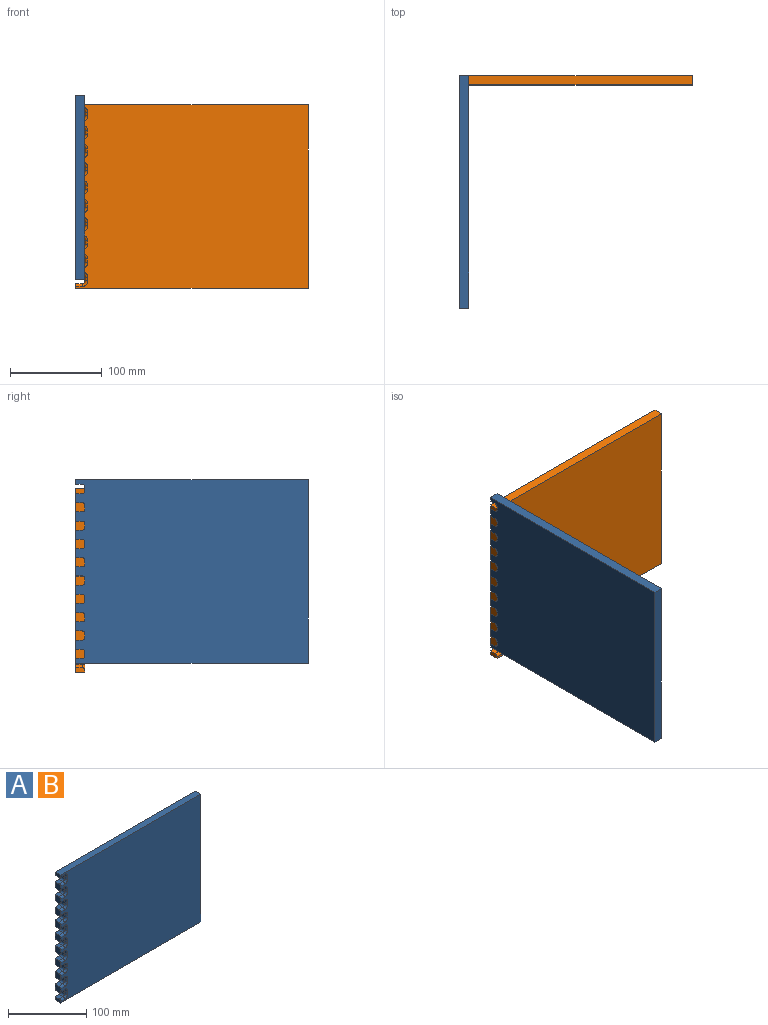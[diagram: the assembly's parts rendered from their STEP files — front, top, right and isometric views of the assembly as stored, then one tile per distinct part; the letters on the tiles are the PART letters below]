
ASSEMBLY  parts=2 mates=1
PART A: 116 faces, bbox 253.6x10x201.6 mm
  f0: plane 10x10mm, normal (-1,0,0), area 96.1mm2, adj f7,f8,f13,f21,f100,f101
  f1: cylinder r=3mm len=7mm, axis (0,1,0), area 33mm2, adj f3,f9,f10,f101
  f2: cylinder r=3mm len=7mm, axis (1,0,0), area 33mm2, adj f3,f10,f99,f100
  f3: torus R=6mm, axis (0,-1,0), area 30.3mm2, adj f1,f2,f5,f100
  f4: cylinder r=3mm len=7mm, axis (0,-1,0), area 33mm2, adj f6,f8,f9,f101
  f5: cylinder r=3mm len=4mm, axis (0,0,-1), area 18.8mm2, adj f3,f6,f9,f100
  f6: torus R=6mm, axis (0,-1,0), area 30.3mm2, adj f4,f5,f7,f100
  f7: cylinder r=3mm len=7mm, axis (-1,0,0), area 33mm2, adj f0,f6,f8,f100
  f8: plane 7x7mm, normal (0,0,1), area 49mm2, adj f0,f4,f7,f101
  f9: plane 7x4mm, normal (-1,0,0), area 28mm2, adj f1,f4,f5,f101
  f10: plane 7x7mm, normal (0,0,-1), area 49mm2, adj f1,f2,f99,f101
  f11: plane 10x10mm, normal (-1,0,0), area 96.1mm2, adj f18,f19,f24,f32,f100,f101
  f12: cylinder r=3mm len=7mm, axis (0,1,0), area 33mm2, adj f14,f20,f21,f101
  f13: cylinder r=3mm len=7mm, axis (1,0,0), area 33mm2, adj f0,f14,f21,f100
  f14: torus R=6mm, axis (0,-1,0), area 30.3mm2, adj f12,f13,f16,f100
  f15: cylinder r=3mm len=7mm, axis (0,-1,0), area 33mm2, adj f17,f19,f20,f101
  f16: cylinder r=3mm len=4mm, axis (0,0,-1), area 18.8mm2, adj f14,f17,f20,f100
  f17: torus R=6mm, axis (0,-1,0), area 30.3mm2, adj f15,f16,f18,f100
  f18: cylinder r=3mm len=7mm, axis (-1,0,0), area 33mm2, adj f11,f17,f19,f100
  f19: plane 7x7mm, normal (0,0,1), area 49mm2, adj f11,f15,f18,f101
  f20: plane 7x4mm, normal (-1,0,0), area 28mm2, adj f12,f15,f16,f101
  f21: plane 7x7mm, normal (0,0,-1), area 49mm2, adj f0,f12,f13,f101
  f22: plane 10x10mm, normal (-1,0,0), area 96.1mm2, adj f29,f30,f35,f43,f100,f101
  f23: cylinder r=3mm len=7mm, axis (0,1,0), area 33mm2, adj f25,f31,f32,f101
  f24: cylinder r=3mm len=7mm, axis (1,0,0), area 33mm2, adj f11,f25,f32,f100
  f25: torus R=6mm, axis (0,-1,0), area 30.3mm2, adj f23,f24,f27,f100
  f26: cylinder r=3mm len=7mm, axis (0,-1,0), area 33mm2, adj f28,f30,f31,f101
  f27: cylinder r=3mm len=4mm, axis (0,0,-1), area 18.8mm2, adj f25,f28,f31,f100
  f28: torus R=6mm, axis (0,-1,0), area 30.3mm2, adj f26,f27,f29,f100
  f29: cylinder r=3mm len=7mm, axis (-1,0,0), area 33mm2, adj f22,f28,f30,f100
  f30: plane 7x7mm, normal (0,0,1), area 49mm2, adj f22,f26,f29,f101
  f31: plane 7x4mm, normal (-1,0,0), area 28mm2, adj f23,f26,f27,f101
  f32: plane 7x7mm, normal (0,0,-1), area 49mm2, adj f11,f23,f24,f101
  f33: plane 10x10mm, normal (-1,0,0), area 96.1mm2, adj f40,f41,f46,f54,f100,f101
  f34: cylinder r=3mm len=7mm, axis (0,1,0), area 33mm2, adj f36,f42,f43,f101
  f35: cylinder r=3mm len=7mm, axis (1,0,0), area 33mm2, adj f22,f36,f43,f100
  f36: torus R=6mm, axis (0,-1,0), area 30.3mm2, adj f34,f35,f38,f100
  f37: cylinder r=3mm len=7mm, axis (0,-1,0), area 33mm2, adj f39,f41,f42,f101
  f38: cylinder r=3mm len=4mm, axis (0,0,-1), area 18.8mm2, adj f36,f39,f42,f100
  f39: torus R=6mm, axis (0,-1,0), area 30.3mm2, adj f37,f38,f40,f100
  f40: cylinder r=3mm len=7mm, axis (-1,0,0), area 33mm2, adj f33,f39,f41,f100
  f41: plane 7x7mm, normal (0,0,1), area 49mm2, adj f33,f37,f40,f101
  f42: plane 7x4mm, normal (-1,0,0), area 28mm2, adj f34,f37,f38,f101
  f43: plane 7x7mm, normal (0,0,-1), area 49mm2, adj f22,f34,f35,f101
  f44: plane 10x10mm, normal (-1,0,0), area 96.1mm2, adj f51,f52,f57,f65,f100,f101
  f45: cylinder r=3mm len=7mm, axis (0,1,0), area 33mm2, adj f47,f53,f54,f101
  f46: cylinder r=3mm len=7mm, axis (1,0,0), area 33mm2, adj f33,f47,f54,f100
  f47: torus R=6mm, axis (0,-1,0), area 30.3mm2, adj f45,f46,f49,f100
  f48: cylinder r=3mm len=7mm, axis (0,-1,0), area 33mm2, adj f50,f52,f53,f101
  f49: cylinder r=3mm len=4mm, axis (0,0,-1), area 18.8mm2, adj f47,f50,f53,f100
  f50: torus R=6mm, axis (0,-1,0), area 30.3mm2, adj f48,f49,f51,f100
  f51: cylinder r=3mm len=7mm, axis (-1,0,0), area 33mm2, adj f44,f50,f52,f100
  f52: plane 7x7mm, normal (0,0,1), area 49mm2, adj f44,f48,f51,f101
  f53: plane 7x4mm, normal (-1,0,0), area 28mm2, adj f45,f48,f49,f101
  f54: plane 7x7mm, normal (0,0,-1), area 49mm2, adj f33,f45,f46,f101
  f55: plane 10x10mm, normal (-1,0,0), area 96.1mm2, adj f62,f63,f68,f76,f100,f101
  f56: cylinder r=3mm len=7mm, axis (0,1,0), area 33mm2, adj f58,f64,f65,f101
  f57: cylinder r=3mm len=7mm, axis (1,0,0), area 33mm2, adj f44,f58,f65,f100
  f58: torus R=6mm, axis (0,-1,0), area 30.3mm2, adj f56,f57,f60,f100
  f59: cylinder r=3mm len=7mm, axis (0,-1,0), area 33mm2, adj f61,f63,f64,f101
  f60: cylinder r=3mm len=4mm, axis (0,0,-1), area 18.8mm2, adj f58,f61,f64,f100
  f61: torus R=6mm, axis (0,-1,0), area 30.3mm2, adj f59,f60,f62,f100
  f62: cylinder r=3mm len=7mm, axis (-1,0,0), area 33mm2, adj f55,f61,f63,f100
  f63: plane 7x7mm, normal (0,0,1), area 49mm2, adj f55,f59,f62,f101
  f64: plane 7x4mm, normal (-1,0,0), area 28mm2, adj f56,f59,f60,f101
  f65: plane 7x7mm, normal (0,0,-1), area 49mm2, adj f44,f56,f57,f101
  f66: plane 10x10mm, normal (-1,0,0), area 96.1mm2, adj f73,f74,f79,f87,f100,f101
  f67: cylinder r=3mm len=7mm, axis (0,1,0), area 33mm2, adj f69,f75,f76,f101
  f68: cylinder r=3mm len=7mm, axis (1,0,0), area 33mm2, adj f55,f69,f76,f100
  f69: torus R=6mm, axis (0,-1,0), area 30.3mm2, adj f67,f68,f71,f100
  f70: cylinder r=3mm len=7mm, axis (0,-1,0), area 33mm2, adj f72,f74,f75,f101
  f71: cylinder r=3mm len=4mm, axis (0,0,-1), area 18.8mm2, adj f69,f72,f75,f100
  f72: torus R=6mm, axis (0,-1,0), area 30.3mm2, adj f70,f71,f73,f100
  f73: cylinder r=3mm len=7mm, axis (-1,0,0), area 33mm2, adj f66,f72,f74,f100
  f74: plane 7x7mm, normal (0,0,1), area 49mm2, adj f66,f70,f73,f101
  f75: plane 7x4mm, normal (-1,0,0), area 28mm2, adj f67,f70,f71,f101
  f76: plane 7x7mm, normal (0,0,-1), area 49mm2, adj f55,f67,f68,f101
  f77: plane 10x10mm, normal (-1,0,0), area 96.1mm2, adj f84,f85,f90,f98,f100,f101
  f78: cylinder r=3mm len=7mm, axis (0,1,0), area 33mm2, adj f80,f86,f87,f101
  f79: cylinder r=3mm len=7mm, axis (1,0,0), area 33mm2, adj f66,f80,f87,f100
  f80: torus R=6mm, axis (0,-1,0), area 30.3mm2, adj f78,f79,f82,f100
  f81: cylinder r=3mm len=7mm, axis (0,-1,0), area 33mm2, adj f83,f85,f86,f101
  f82: cylinder r=3mm len=4mm, axis (0,0,-1), area 18.8mm2, adj f80,f83,f86,f100
  f83: torus R=6mm, axis (0,-1,0), area 30.3mm2, adj f81,f82,f84,f100
  f84: cylinder r=3mm len=7mm, axis (-1,0,0), area 33mm2, adj f77,f83,f85,f100
  f85: plane 7x7mm, normal (0,0,1), area 49mm2, adj f77,f81,f84,f101
  f86: plane 7x4mm, normal (-1,0,0), area 28mm2, adj f78,f81,f82,f101
  f87: plane 7x7mm, normal (0,0,-1), area 49mm2, adj f66,f78,f79,f101
  f88: plane 10x10mm, normal (-1,0,0), area 96.1mm2, adj f95,f96,f100,f101,f108,f110
  f89: cylinder r=3mm len=7mm, axis (0,1,0), area 33mm2, adj f91,f97,f98,f101
  f90: cylinder r=3mm len=7mm, axis (1,0,0), area 33mm2, adj f77,f91,f98,f100
  f91: torus R=6mm, axis (0,-1,0), area 30.3mm2, adj f89,f90,f93,f100
  f92: cylinder r=3mm len=7mm, axis (0,-1,0), area 33mm2, adj f94,f96,f97,f101
  f93: cylinder r=3mm len=4mm, axis (0,0,-1), area 18.8mm2, adj f91,f94,f97,f100
  f94: torus R=6mm, axis (0,-1,0), area 30.3mm2, adj f92,f93,f95,f100
  f95: cylinder r=3mm len=7mm, axis (-1,0,0), area 33mm2, adj f88,f94,f96,f100
  f96: plane 7x7mm, normal (0,0,1), area 49mm2, adj f88,f92,f95,f101
  f97: plane 7x4mm, normal (-1,0,0), area 28mm2, adj f89,f92,f93,f101
  f98: plane 7x7mm, normal (0,0,-1), area 49mm2, adj f77,f89,f90,f101
  f99: plane 10x5mm, normal (-1,0,0), area 48.1mm2, adj f2,f10,f100,f101,f104
  f100: plane 253.61x200mm, normal (0,-1,0), area 48796.1mm2, adj f0,f2,f3,f5,f6,f7,f11,f13
  f101: plane 253.61x200mm, normal (0,1,0), area 49760.2mm2, adj f0,f1,f4,f8,f9,f10,f11,f12
  f102: plane 253.61x10mm, normal (0,0,-1), area 2536.1mm2, adj f100,f101,f103,f105
  f103: plane 200x10mm, normal (1,0,0), area 2000mm2, adj f100,f101,f102,f104
  f104: plane 253.61x10mm, normal (0,0,1), area 2536.1mm2, adj f99,f100,f101,f103
  f105: plane 10x5mm, normal (-1,0,0), area 48.1mm2, adj f100,f101,f102,f106,f115
  f106: plane 7x7mm, normal (0,0,1), area 49mm2, adj f101,f105,f112,f115
  f107: plane 7x4mm, normal (-1,0,0), area 28mm2, adj f101,f109,f112,f113
  f108: plane 7x7mm, normal (0,0,-1), area 49mm2, adj f88,f101,f109,f110
  f109: cylinder r=3mm len=7mm, axis (0,1,0), area 33mm2, adj f101,f107,f108,f111
  f110: cylinder r=3mm len=7mm, axis (1,0,0), area 33mm2, adj f88,f100,f108,f111
  f111: torus R=6mm, axis (0,-1,0), area 30.3mm2, adj f100,f109,f110,f113
  f112: cylinder r=3mm len=7mm, axis (0,-1,0), area 33mm2, adj f101,f106,f107,f114
  f113: cylinder r=3mm len=4mm, axis (0,0,-1), area 18.8mm2, adj f100,f107,f111,f114
  f114: torus R=6mm, axis (0,-1,0), area 30.3mm2, adj f100,f112,f113,f115
  f115: cylinder r=3mm len=7mm, axis (-1,0,0), area 33mm2, adj f100,f105,f106,f114
PART B: same geometry as A
PLACE A rot(axis=(-0.71,0.71,0),180deg) t=(-315.47,-72.96,-0.67)mm
PLACE B t=(-315.47,-72.96,-172.23)mm
MATE fastened A.f101 <-> B.f88  axis (-1,0,0) through (-315.47,-72.96,-176.45)mm
